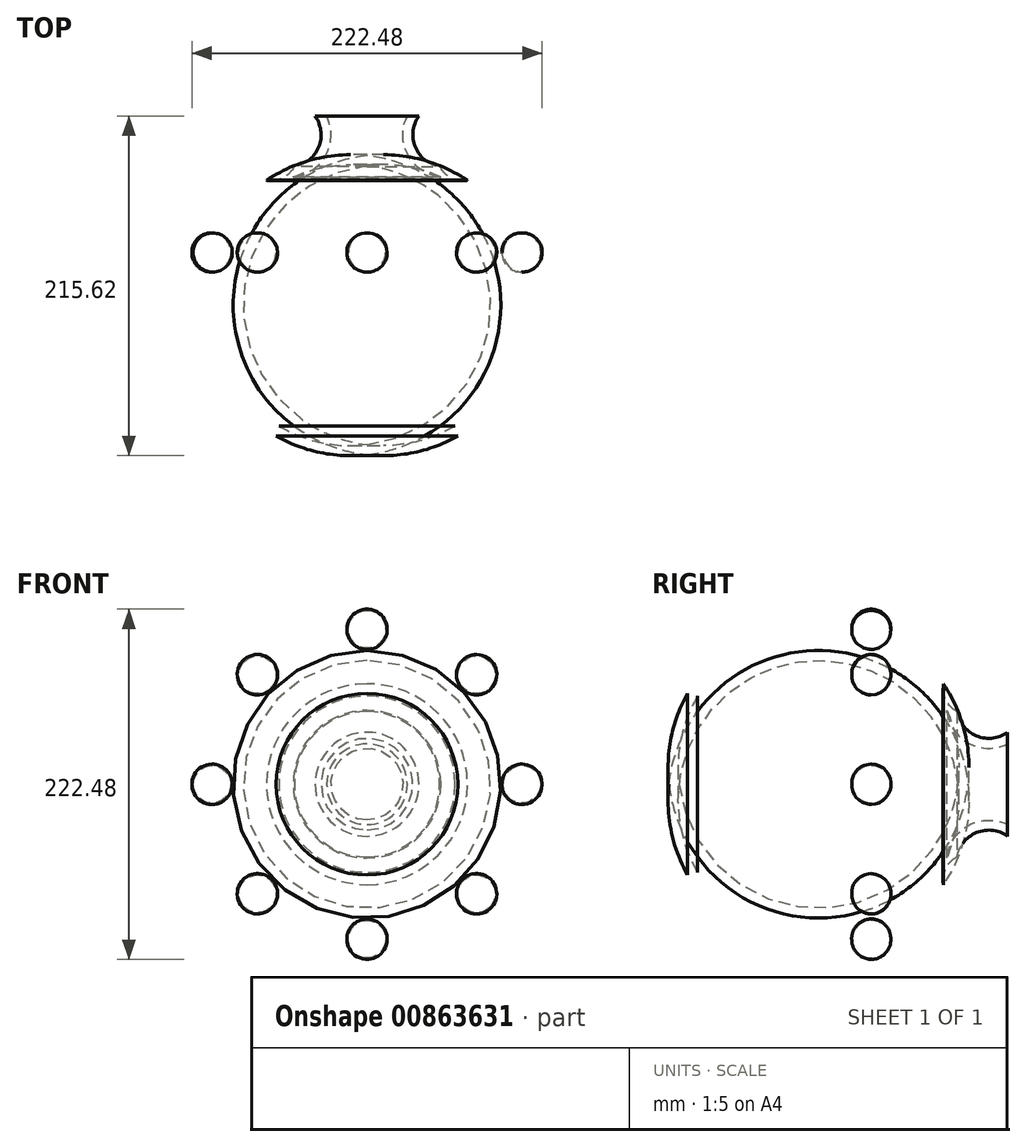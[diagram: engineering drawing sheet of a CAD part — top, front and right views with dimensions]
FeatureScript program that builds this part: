
annotation { "Feature Type Name" : "Feature", "Feature Type Description" : "" }
export const myFeature = defineFeature(function(context is Context, id is Id, definition is map)
    precondition{}
    {
        {
            var Q0;
            Q0=qCreatedBy(makeId("Top.planeOp"),FACE);
            var sketch = newSketch(context, id + "F0", { "sketchPlane" : qUnion([Q0])});
            skLineSegment(sketch, "E0", {"start": v(0, -92.12) * mm, "end": v(0, 111.08) * mm});
            skLineSegment(sketch, "E1", {"start": v(0, 111.08) * mm, "end": v(29.9, 111.08) * mm});
            skArc(sketch, "E2", {"start": v(32.99, 111.08) * mm, "mid": v(31.16, 90.33) * mm, "end": v(48.45, 78.71) * mm});
            skArc(sketch, "E3", {"start": v(57.7, -92.12) * mm, "mid": v(105.98, -3.84) * mm, "end": v(48.45, 78.71) * mm});
            skLineSegment(sketch, "E4", {"start": v(0, -92.12) * mm, "end": v(57.7, -92.12) * mm});
            skLineSegment(sketch, "E5", {"start": v(29.9, 111.08) * mm, "end": v(32.99, 111.08) * mm});
            skSolve(sketch);
        }
        {
            var Q0;
            Q0=makeQuery(id+"F0.imprint","IMPRINT",FACE,{"disambiguationData":[TD([[makeQuery(id+"F0.imprint","IMPRINT",EDGE,{"derivedFrom":sQuery(id+"F0.wireOp",EDGE,"E0")}),-1.0]])]});
            var Q1;
            Q1=sQuery(id+"F0.wireOp",EDGE,"E0");
            revolve(context, id + "F1", {"surfaceOperationType" : NewSurfaceOperationType.NEW, "entities" : qUnion([Q0]), "axis" : qUnion([Q1]), "revolveType" : RevolveType.FULL});
        }
        {
            var Q0;
            Q0=qCreatedBy(makeId("Top.planeOp"),FACE);
            var sketch = newSketch(context, id + "F2", { "sketchPlane" : qUnion([Q0])});
            skArc(sketch, "E6", {"start": v(115.09, 34.95) * mm, "mid": v(127.5, 47.78) * mm, "end": v(114.25, 59.75) * mm});
            skLineSegment(sketch, "E7", {"start": v(114.25, 59.75) * mm, "end": v(115.09, 34.95) * mm});
            skSolve(sketch);
        }
        {
            var Q0;
            Q0=makeQuery(id+"F2.imprint","IMPRINT",FACE,{"disambiguationData":[TD([[makeQuery(id+"F2.imprint","IMPRINT",EDGE,{"derivedFrom":sQuery(id+"F2.wireOp",EDGE,"E6")}),1.0]])]});
            var Q1;
            Q1=sQuery(id+"F2.wireOp",EDGE,"E7");
            revolve(context, id + "F3", {"surfaceOperationType" : NewSurfaceOperationType.NEW, "entities" : qUnion([Q0]), "axis" : qUnion([Q1]), "revolveType" : RevolveType.FULL});
        }
        {
            var Q0;
            Q0=makeQuery(id+"F3.opRevolve","SWEPT_BODY",BODY,{"disambiguationData":[OSD([sQuery(id+"F2.wireOp",EDGE,"E6"),sQuery(id+"F2.wireOp",EDGE,"E7")])]});
            transform(context, id + "F4", {"entities" : qUnion([Q0]), "transformType" : TransformType.TRANSLATION_3D, "dx" : -16.26 * mm, "dy" : -22.86 * mm, "dz" : 0 * mm, "makeCopy" : false});
        }
        {
            var Q0;
            Q0=makeQuery(id+"F3.opRevolve","SWEPT_BODY",BODY,{"disambiguationData":[OSD([sQuery(id+"F2.wireOp",EDGE,"E6"),sQuery(id+"F2.wireOp",EDGE,"E7")])]});
            var Q1;
            Q1=makeQuery(id+"F1.opRevolve","SWEPT_FACE",FACE,{"disambiguationData":[OSD([sQuery(id+"F0.wireOp",EDGE,"E3")])]});
            circularPattern(context, id + "F5", {"entities" : qUnion([Q0]), "axis" : qUnion([Q1]), "angle" : 360 * degree, "instanceCount" : 8, "equalSpace" : true});
        }
        {
            var Q0;
            Q0=qCreatedBy(makeId("Top.planeOp"),FACE);
            var sketch = newSketch(context, id + "F6", { "sketchPlane" : qUnion([Q0])});
            skCircle(sketch, "E8", {"center": v(60.87, 86.65) * mm, "radius": 16.58 * mm});
            skSolve(sketch);
        }
        {
            var Q0;
            Q0=makeQuery(id+"F1.opRevolve","SWEPT_FACE",FACE,{"disambiguationData":[OSD([sQuery(id+"F0.wireOp",EDGE,"E1"),sQuery(id+"F0.wireOp",EDGE,"E5")])]});
            shell(context, id + "F7", {"entities" : qUnion([Q0]), "thickness" : 6.35 * mm});
        }
        {
            var Q0;
            Q0=makeQuery(id+"F6.imprint","IMPRINT",FACE,{"disambiguationData":[TD([[makeQuery(id+"F6.imprint","IMPRINT",EDGE,{"derivedFrom":sQuery(id+"F6.wireOp",EDGE,"E8")}),1.0]])]});
            var Q1;
            Q1=makeQuery(id+"F1.opRevolve","SWEPT_FACE",FACE,{"disambiguationData":[OSD([sQuery(id+"F0.wireOp",EDGE,"E2")])]});
            revolve(context, id + "F8", {"operationType" : NewBodyOperationType.REMOVE, "surfaceOperationType" : NewSurfaceOperationType.NEW, "entities" : qUnion([Q0]), "axis" : qUnion([Q1]), "revolveType" : RevolveType.FULL, "oppositeDirection" : true});
        }
        {
            var Q0;
            Q0=qCreatedBy(makeId("Top.planeOp"),FACE);
            var sketch = newSketch(context, id + "F9", { "sketchPlane" : qUnion([Q0])});
            skArc(sketch, "E9", {"start": v(-69.44, 104.64) * mm, "mid": v(-79.8, 93.64) * mm, "end": v(-69.01, 83.06) * mm});
            skLineSegment(sketch, "E10", {"start": v(-69.44, 104.64) * mm, "end": v(-69.01, 83.06) * mm});
            skSolve(sketch);
        }
        {
            var Q0;
            Q0=makeQuery(id+"F9.imprint","IMPRINT",FACE,{"disambiguationData":[TD([[makeQuery(id+"F9.imprint","IMPRINT",EDGE,{"derivedFrom":sQuery(id+"F9.wireOp",EDGE,"E9")}),1.0]])]});
            var Q1;
            Q1=sQuery(id+"F9.wireOp",EDGE,"E10");
            revolve(context, id + "F10", {"surfaceOperationType" : NewSurfaceOperationType.NEW, "entities" : qUnion([Q0]), "axis" : qUnion([Q1]), "revolveType" : RevolveType.FULL});
        }
        {
            var Q0;
            Q0=makeQuery(id+"F10.opRevolve","SWEPT_BODY",BODY,{"disambiguationData":[OSD([sQuery(id+"F9.wireOp",EDGE,"E9"),sQuery(id+"F9.wireOp",EDGE,"E10")])]});
            transform(context, id + "F11", {"entities" : qUnion([Q0]), "transformType" : TransformType.TRANSLATION_3D, "dx" : 35.81 * mm, "dy" : 0 * mm, "dz" : 0 * mm, "makeCopy" : false});
        }
        {
            var Q0;
            Q0=makeQuery(id+"F10.opRevolve","SWEPT_BODY",BODY,{"disambiguationData":[OSD([sQuery(id+"F9.wireOp",EDGE,"E9"),sQuery(id+"F9.wireOp",EDGE,"E10")])]});
            var Q1;
            Q1=makeQuery(id+"F1.opRevolve","SWEPT_FACE",FACE,{"disambiguationData":[OSD([sQuery(id+"F0.wireOp",EDGE,"E2")])]});
            circularPattern(context, id + "F12", {"entities" : qUnion([Q0]), "axis" : qUnion([Q1]), "angle" : 360 * degree, "instanceCount" : 8, "equalSpace" : true});
        }
        {
            var Q0;
            Q0=makeQuery(id+"F12.opPattern","COPY",BODY,{"derivedFrom":makeQuery(id+"F10.opRevolve","SWEPT_BODY",BODY,{"disambiguationData":[OSD([sQuery(id+"F9.wireOp",EDGE,"E9"),sQuery(id+"F9.wireOp",EDGE,"E10")])]}),"instanceName":"1"});
            var Q1;
            Q1=makeQuery(id+"F12.opPattern","COPY",BODY,{"derivedFrom":makeQuery(id+"F10.opRevolve","SWEPT_BODY",BODY,{"disambiguationData":[OSD([sQuery(id+"F9.wireOp",EDGE,"E9"),sQuery(id+"F9.wireOp",EDGE,"E10")])]}),"instanceName":"2"});
            var Q2;
            Q2=makeQuery(id+"F12.opPattern","COPY",BODY,{"derivedFrom":makeQuery(id+"F10.opRevolve","SWEPT_BODY",BODY,{"disambiguationData":[OSD([sQuery(id+"F9.wireOp",EDGE,"E9"),sQuery(id+"F9.wireOp",EDGE,"E10")])]}),"instanceName":"3"});
            var Q3;
            Q3=makeQuery(id+"F12.opPattern","COPY",BODY,{"derivedFrom":makeQuery(id+"F10.opRevolve","SWEPT_BODY",BODY,{"disambiguationData":[OSD([sQuery(id+"F9.wireOp",EDGE,"E9"),sQuery(id+"F9.wireOp",EDGE,"E10")])]}),"instanceName":"4"});
            var Q4;
            Q4=makeQuery(id+"F12.opPattern","COPY",BODY,{"derivedFrom":makeQuery(id+"F10.opRevolve","SWEPT_BODY",BODY,{"disambiguationData":[OSD([sQuery(id+"F9.wireOp",EDGE,"E9"),sQuery(id+"F9.wireOp",EDGE,"E10")])]}),"instanceName":"6"});
            var Q5;
            Q5=makeQuery(id+"F10.opRevolve","SWEPT_BODY",BODY,{"disambiguationData":[OSD([sQuery(id+"F9.wireOp",EDGE,"E9"),sQuery(id+"F9.wireOp",EDGE,"E10")])]});
            var Q6;
            Q6=makeQuery(id+"F12.opPattern","COPY",BODY,{"derivedFrom":makeQuery(id+"F10.opRevolve","SWEPT_BODY",BODY,{"disambiguationData":[OSD([sQuery(id+"F9.wireOp",EDGE,"E9"),sQuery(id+"F9.wireOp",EDGE,"E10")])]}),"instanceName":"7"});
            var Q7;
            Q7=makeQuery(id+"F12.opPattern","COPY",BODY,{"derivedFrom":makeQuery(id+"F10.opRevolve","SWEPT_BODY",BODY,{"disambiguationData":[OSD([sQuery(id+"F9.wireOp",EDGE,"E9"),sQuery(id+"F9.wireOp",EDGE,"E10")])]}),"instanceName":"5"});
            var Q8;
            Q8=makeQuery(id+"F3.opRevolve","SWEPT_BODY",BODY,{"disambiguationData":[OSD([sQuery(id+"F2.wireOp",EDGE,"E6"),sQuery(id+"F2.wireOp",EDGE,"E7")])]});
            booleanBodies(context, id + "F13", {"operationType" : BooleanOperationType.SUBTRACTION, "tools" : qUnion([Q0, Q1, Q2, Q3, Q4, Q5, Q6, Q7]), "targets" : qUnion([Q8])});
        }
    });
